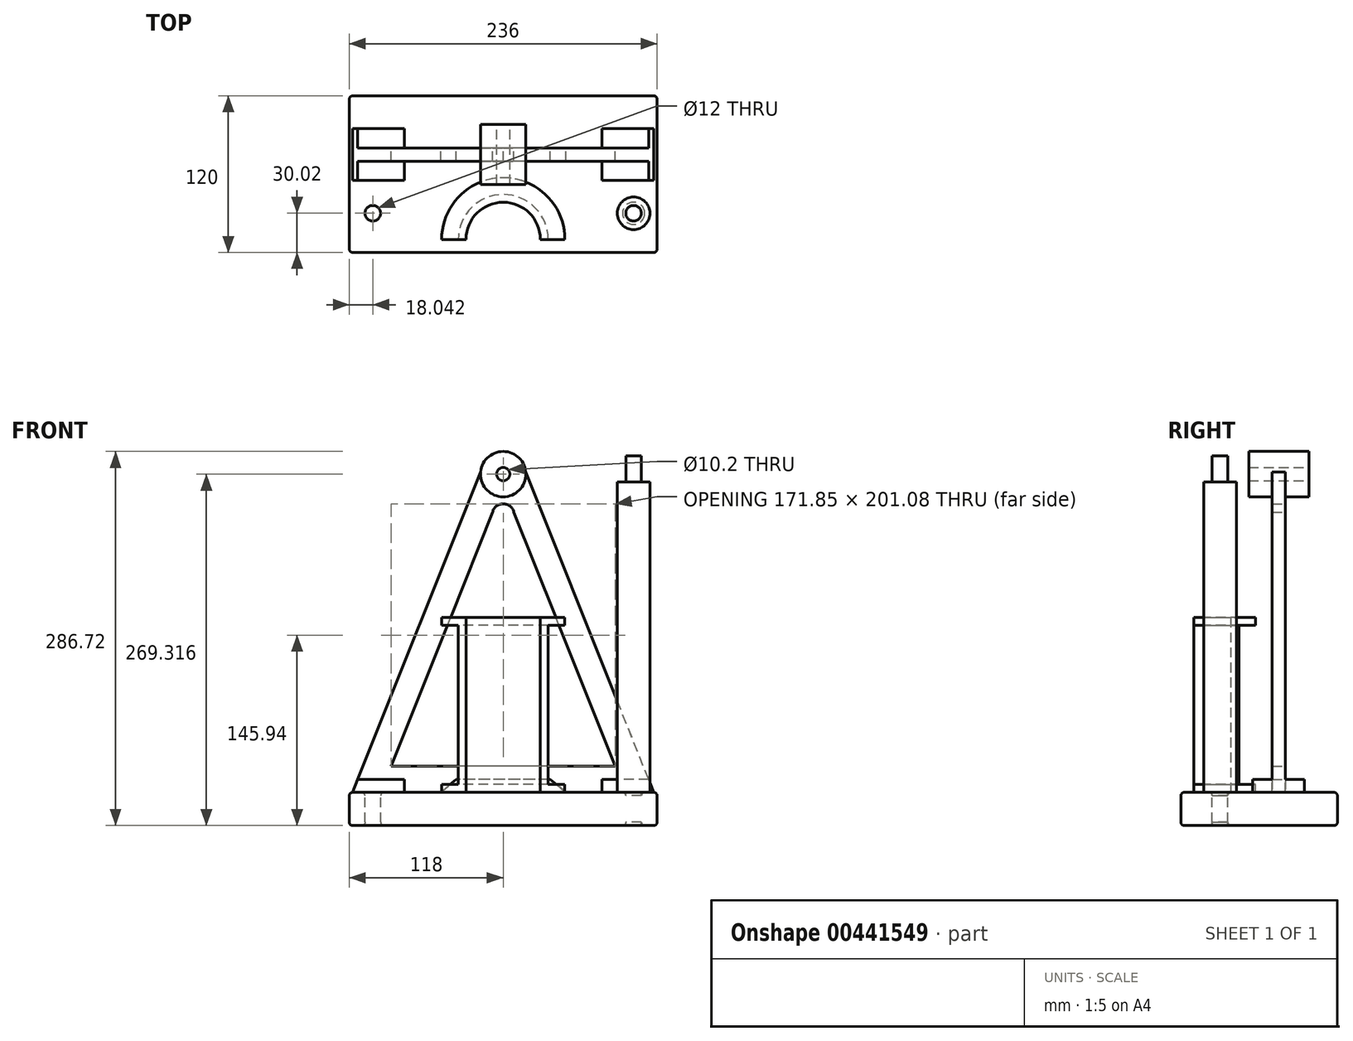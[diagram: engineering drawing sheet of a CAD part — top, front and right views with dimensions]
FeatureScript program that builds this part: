
annotation { "Feature Type Name" : "Feature", "Feature Type Description" : "" }
export const myFeature = defineFeature(function(context is Context, id is Id, definition is map)
    precondition{}
    {
        {
            var Q0;
            Q0=qCreatedBy(makeId("Top.planeOp"),FACE);
            var sketch = newSketch(context, id + "F0", { "sketchPlane" : qUnion([Q0])});
            skLineSegment(sketch, "E0.bottom", {"start": v(118, -60) * mm, "end": v(-118, -60) * mm});
            skLineSegment(sketch, "E0.top", {"start": v(118, 60) * mm, "end": v(-118, 60) * mm});
            skLineSegment(sketch, "E0.left", {"start": v(118, -60) * mm, "end": v(118, 60) * mm});
            skLineSegment(sketch, "E0.right", {"start": v(-118, -60) * mm, "end": v(-118, 60) * mm});
            skPoint(sketch, "E0.middle", {"position": v(0, 0) * mm});
            skSolve(sketch);
        }
        {
            var Q0;
            Q0 = qSketchRegion(id + "F0", true);
            extrude(context, id + "F1", {"entities" : qUnion([Q0]), "depth" : 25.4 * mm});
        }
        {
            var Q0;
            Q0=makeQuery(id+"F1.opExtrude","CAP_FACE",FACE,{"disambiguationData":[OSD([sQuery(id+"F0.wireOp",EDGE,"E0.bottom"),sQuery(id+"F0.wireOp",EDGE,"E0.top"),sQuery(id+"F0.wireOp",EDGE,"E0.left"),sQuery(id+"F0.wireOp",EDGE,"E0.right")])],"isStart":false});
            var sketch = newSketch(context, id + "F2", { "sketchPlane" : qUnion([Q0])});
            skCircle(sketch, "E1", {"center": v(-99.96, -29.98) * mm, "radius": 6 * mm});
            skCircle(sketch, "E2", {"center": v(99.96, -29.98) * mm, "radius": 6 * mm});
            skSolve(sketch);
        }
        {
            var Q0;
            Q0 = qSketchRegion(id + "F2", true);
            extrude(context, id + "F3", {"entities" : qUnion([Q0]), "operationType" : NewBodyOperationType.REMOVE, "oppositeDirection" : true, "depth" : 40.4 * mm});
        }
        {
            var Q0;
            Q0=makeQuery(id+"F1.opExtrude","CAP_EDGE",EDGE,{"disambiguationData":[OSD([sQuery(id+"F0.wireOp",EDGE,"E0.bottom")])],"isStart":false});
            var Q1;
            Q1=makeQuery(id+"F1.opExtrude","CAP_EDGE",EDGE,{"disambiguationData":[OSD([sQuery(id+"F0.wireOp",EDGE,"E0.left")])],"isStart":false});
            var Q2;
            Q2=makeQuery(id+"F1.opExtrude","CAP_EDGE",EDGE,{"disambiguationData":[OSD([sQuery(id+"F0.wireOp",EDGE,"E0.top")])],"isStart":false});
            var Q3;
            Q3=makeQuery(id+"F1.opExtrude","SWEPT_FACE",FACE,{"disambiguationData":[OSD([sQuery(id+"F0.wireOp",EDGE,"E0.bottom")])]});
            var Q4;
            Q4=makeQuery(id+"F1.opExtrude","CAP_FACE",FACE,{"disambiguationData":[OSD([sQuery(id+"F0.wireOp",EDGE,"E0.bottom"),sQuery(id+"F0.wireOp",EDGE,"E0.top"),sQuery(id+"F0.wireOp",EDGE,"E0.left"),sQuery(id+"F0.wireOp",EDGE,"E0.right")])],"isStart":true});
            var Q5;
            Q5=makeQuery(id+"F1.opExtrude","SWEPT_FACE",FACE,{"disambiguationData":[OSD([sQuery(id+"F0.wireOp",EDGE,"E0.right")])]});
            var Q6;
            Q6=makeQuery(id+"F1.opExtrude","SWEPT_FACE",FACE,{"disambiguationData":[OSD([sQuery(id+"F0.wireOp",EDGE,"E0.top")])]});
            var Q7;
            Q7=makeQuery(id+"F3.boolean.opBoolean","COPY",FACE,{"derivedFrom":makeQuery(id+"F3.opExtrude","SWEPT_FACE",FACE,{"disambiguationData":[OSD([sQuery(id+"F2.wireOp",EDGE,"E2")])]})});
            var Q8;
            Q8=makeQuery(id+"F3.boolean.opBoolean","COPY",FACE,{"derivedFrom":makeQuery(id+"F3.opExtrude","SWEPT_FACE",FACE,{"disambiguationData":[OSD([sQuery(id+"F2.wireOp",EDGE,"E1")])]})});
            fillet(context, id + "F4", {"entities" : qUnion([Q0, Q1, Q2, Q3, Q4, Q5, Q6, Q7, Q8]), "radius" : 2.54 * mm, "tangentPropagation" : true, "allowEdgeOverflow" : false});
        }
        {
            var Q0;
            Q0=makeQuery(id+"F1.opExtrude","SWEPT_FACE",FACE,{"disambiguationData":[OSD([sQuery(id+"F0.wireOp",EDGE,"E0.top")])]});
            cPlane(context, id + "F5", {"entities" : qUnion([Q0]), "cplaneType" : CPlaneType.OFFSET, "offset" : 40 * mm, "oppositeDirection" : true, "width" : 152.4 * mm, "height" : 152.4 * mm});
        }
        {
            var Q0;
            Q0=qCreatedBy(id+"F5.planeOp",FACE);
            var sketch = newSketch(context, id + "F6", { "sketchPlane" : qUnion([Q0])});
            skLineSegment(sketch, "E3.0", {"start": v(-115.46, 25.4) * mm, "end": v(115.46, 25.4) * mm});
            skArc(sketch, "E4.0", {"start": v(118, 22.86) * mm, "mid": v(117.26, 24.66) * mm, "end": v(115.46, 25.4) * mm});
            skLineSegment(sketch, "E5.0", {"start": v(118, 22.86) * mm, "end": v(118, 2.54) * mm});
            skLineSegment(sketch, "E6", {"start": v(-115.46, 25.4) * mm, "end": v(-17.33, 270.86) * mm});
            skLineSegment(sketch, "E7", {"start": v(-115.46, 25.4) * mm, "end": v(-47.96, 25.4) * mm});
            skLineSegment(sketch, "E8", {"start": v(-47.96, 25.4) * mm, "end": v(-36, 35.44) * mm});
            skLineSegment(sketch, "E9", {"start": v(-36, 35.44) * mm, "end": v(0, 35.44) * mm});
            skLineSegment(sketch, "E10", {"start": v(0, 330.43) * mm, "end": v(0, -58.87) * mm, "construction": true});
            skLineSegment(sketch, "E11", {"start": v(0, 35.44) * mm, "end": v(0, 25.4) * mm});
            skLineSegment(sketch, "E12", {"start": v(0, 25.4) * mm, "end": v(-47.96, 25.4) * mm});
            skPoint(sketch, "E13.orphan", {"position": v(0, 136.47) * mm});
            skLineSegment(sketch, "E14.MirrorCS", {"start": v(115.46, 25.4) * mm, "end": v(17.33, 270.86) * mm});
            skLineSegment(sketch, "E15.MirrorCS", {"start": v(115.46, 25.4) * mm, "end": v(47.96, 25.4) * mm});
            skLineSegment(sketch, "E16.MirrorCS", {"start": v(47.96, 25.4) * mm, "end": v(36, 35.44) * mm});
            skLineSegment(sketch, "E17.MirrorCS", {"start": v(36, 35.44) * mm, "end": v(0, 35.44) * mm});
            skLineSegment(sketch, "E18", {"start": v(0, 45.4) * mm, "end": v(-85.93, 45.4) * mm});
            skLineSegment(sketch, "E19", {"start": v(-85.93, 45.4) * mm, "end": v(-6.89, 243.1) * mm});
            skPoint(sketch, "E20", {"position": v(-8.05, 240.2) * mm});
            skArc(sketch, "E21", {"start": v(0, 246.48) * mm, "mid": v(-5.23, 244.89) * mm, "end": v(-8.05, 240.2) * mm});
            skLineSegment(sketch, "E22.MirrorCS", {"start": v(85.93, 45.4) * mm, "end": v(6.89, 243.1) * mm});
            skLineSegment(sketch, "E23.MirrorCS", {"start": v(0, 45.4) * mm, "end": v(85.93, 45.4) * mm});
            skArc(sketch, "E24.MirrorCS", {"start": v(0, 246.48) * mm, "mid": v(5.23, 244.89) * mm, "end": v(8.05, 240.2) * mm});
            skPoint(sketch, "E25", {"position": v(0, 269.32) * mm});
            skCircle(sketch, "E26", {"center": v(0, 269.32) * mm, "radius": 17.4 * mm});
            skCircle(sketch, "E27", {"center": v(0, 269.32) * mm, "radius": 5.1 * mm});
            skPoint(sketch, "E28.orphan", {"position": v(-13.62, 280.14) * mm});
            skPoint(sketch, "E29.orphan", {"position": v(13.62, 280.14) * mm});
            skLineSegment(sketch, "E30", {"start": v(-111.5, 35.3) * mm, "end": v(-75.6, 35.3) * mm});
            skLineSegment(sketch, "E31", {"start": v(-75.6, 35.3) * mm, "end": v(-75.6, 25.4) * mm});
            skLineSegment(sketch, "E32.MirrorCS", {"start": v(111.5, 35.3) * mm, "end": v(75.6, 35.3) * mm});
            skLineSegment(sketch, "E33.MirrorCS", {"start": v(75.6, 35.3) * mm, "end": v(75.6, 25.4) * mm});
            skSolve(sketch);
        }
        {
            var Q0;
            Q0=makeQuery(id+"F6.imprint","IMPRINT",FACE,{"disambiguationData":[TD([[makeQuery(id+"F6.imprint","IMPRINT",EDGE,{"derivedFrom":sQuery(id+"F6.wireOp",EDGE,"bef8d0ea-a7d9-4311-90df-f243bc0aed0c.0.0")}),1.0]])]});
            var Q1;
            Q1=makeQuery(id+"F6.imprint","IMPRINT",FACE,{"disambiguationData":[TD([[makeQuery(id+"F6.imprint","IMPRINT",EDGE,{"derivedFrom":sQuery(id+"F6.wireOp",EDGE,"E27")}),-1.0]])]});
            var Q2;
            {var subQ5=sQuery(id+"F6.wireOp",EDGE,"E6");Q2=makeQuery(id+"F6.imprint","IMPRINT",FACE,{"disambiguationData":[TD([[makeQuery(id+"F6.imprint","IMPRINT",EDGE,{"derivedFrom":subQ5}),-1.0]])]});}
            var Q3;
            {var subQ11=sQuery(id+"F6.wireOp",EDGE,"E8");Q3=makeQuery(id+"F6.imprint","IMPRINT",FACE,{"disambiguationData":[TD([[makeQuery(id+"F6.imprint","IMPRINT",EDGE,{"derivedFrom":subQ11}),1.0]])]});}
            var Q4;
            {var subQ3=sQuery(id+"F6.wireOp",EDGE,"E32.MirrorCS");Q4=makeQuery(id+"F6.imprint","IMPRINT",FACE,{"disambiguationData":[TD([[makeQuery(id+"F6.imprint","IMPRINT",EDGE,{"derivedFrom":subQ3}),1.0]])]});}
            extrude(context, id + "F7", {"entities" : qUnion([Q0, Q1, Q2, Q3, Q4]), "oppositeDirection" : true, "depth" : 10 * mm});
        }
        {
            var Q0;
            {var subQ3=sQuery(id+"F6.wireOp",EDGE,"E30");Q0=makeQuery(id+"F6.imprint","IMPRINT",FACE,{"disambiguationData":[TD([[makeQuery(id+"F6.imprint","IMPRINT",EDGE,{"derivedFrom":subQ3}),-1.0]])]});}
            var Q1;
            {var subQ3=sQuery(id+"F6.wireOp",EDGE,"E32.MirrorCS");Q1=makeQuery(id+"F6.imprint","IMPRINT",FACE,{"disambiguationData":[TD([[makeQuery(id+"F6.imprint","IMPRINT",EDGE,{"derivedFrom":subQ3}),1.0]])]});}
            extrude(context, id + "F8", {"entities" : qUnion([Q0, Q1]), "operationType" : NewBodyOperationType.ADD, "depth" : 14.8 * mm});
        }
        {
            var Q0;
            {var subQ3=sQuery(id+"F6.wireOp",EDGE,"E30");Q0=makeQuery(id+"F6.imprint","IMPRINT",FACE,{"disambiguationData":[TD([[makeQuery(id+"F6.imprint","IMPRINT",EDGE,{"derivedFrom":subQ3}),-1.0]])]});}
            var Q1;
            {var subQ3=sQuery(id+"F6.wireOp",EDGE,"E32.MirrorCS");Q1=makeQuery(id+"F6.imprint","IMPRINT",FACE,{"disambiguationData":[TD([[makeQuery(id+"F6.imprint","IMPRINT",EDGE,{"derivedFrom":subQ3}),1.0]])]});}
            extrude(context, id + "F9", {"entities" : qUnion([Q0, Q1]), "operationType" : NewBodyOperationType.ADD, "oppositeDirection" : true, "depth" : 24.9 * mm});
        }
        {
            var Q0;
            Q0=makeQuery(id+"F6.imprint","IMPRINT",FACE,{"disambiguationData":[TD([[makeQuery(id+"F6.imprint","IMPRINT",EDGE,{"derivedFrom":sQuery(id+"F6.wireOp",EDGE,"E27")}),-1.0]])]});
            extrude(context, id + "F10", {"entities" : qUnion([Q0]), "operationType" : NewBodyOperationType.ADD, "depth" : 18 * mm});
        }
        {
            var Q0;
            Q0=makeQuery(id+"F6.imprint","IMPRINT",FACE,{"disambiguationData":[TD([[makeQuery(id+"F6.imprint","IMPRINT",EDGE,{"derivedFrom":sQuery(id+"F6.wireOp",EDGE,"E27")}),-1.0]])]});
            extrude(context, id + "F11", {"entities" : qUnion([Q0]), "operationType" : NewBodyOperationType.ADD, "oppositeDirection" : true, "depth" : 27.94 * mm});
        }
        {
            var Q0;
            Q0=makeQuery(id+"F1.opExtrude","CAP_FACE",FACE,{"disambiguationData":[OSD([sQuery(id+"F0.wireOp",EDGE,"E0.bottom"),sQuery(id+"F0.wireOp",EDGE,"E0.top"),sQuery(id+"F0.wireOp",EDGE,"E0.left"),sQuery(id+"F0.wireOp",EDGE,"E0.right")])],"isStart":false});
            var sketch = newSketch(context, id + "F12", { "sketchPlane" : qUnion([Q0])});
            skCircle(sketch, "E34.0", {"center": v(99.96, -29.98) * mm, "radius": 6 * mm});
            skCircle(sketch, "E35", {"center": v(99.96, -29.98) * mm, "radius": 12.5 * mm});
            skSolve(sketch);
        }
        {
            var Q0;
            Q0 = qSketchRegion(id + "F12", true);
            var Q1;
            Q1=makeQuery(id+"F12.imprint","IMPRINT",FACE,{"disambiguationData":[TD([[makeQuery(id+"F12.imprint","IMPRINT",EDGE,{"derivedFrom":sQuery(id+"F12.wireOp",EDGE,"E34.0")}),1.0]])]});
            extrude(context, id + "F13", {"entities" : qUnion([Q0, Q1]), "depth" : 238 * mm});
        }
        {
            var Q0;
            Q0=makeQuery(id+"F12.imprint","IMPRINT",FACE,{"disambiguationData":[TD([[makeQuery(id+"F12.imprint","IMPRINT",EDGE,{"derivedFrom":sQuery(id+"F12.wireOp",EDGE,"E34.0")}),1.0]])]});
            var Q1;
            Q1=makeQuery(id+"F1.opExtrude","CAP_FACE",FACE,{"disambiguationData":[OSD([sQuery(id+"F0.wireOp",EDGE,"E0.bottom"),sQuery(id+"F0.wireOp",EDGE,"E0.top"),sQuery(id+"F0.wireOp",EDGE,"E0.left"),sQuery(id+"F0.wireOp",EDGE,"E0.right")])],"isStart":true});
            extrude(context, id + "F14", {"entities" : qUnion([Q0]), "operationType" : NewBodyOperationType.ADD, "endBound" : BoundingType.UP_TO_SURFACE, "oppositeDirection" : true, "endBoundEntityFace" : qUnion([Q1]), "depth" : 25.4 * mm});
        }
        {
            var Q0;
            Q0=makeQuery(id+"F13.opExtrude","CAP_FACE",FACE,{"disambiguationData":[OSD([sQuery(id+"F12.wireOp",EDGE,"E35")])],"isStart":false});
            var sketch = newSketch(context, id + "F15", { "sketchPlane" : qUnion([Q0])});
            skCircle(sketch, "E36.0", {"center": v(99.96, -29.98) * mm, "radius": 6 * mm});
            skSolve(sketch);
        }
        {
            var Q0;
            Q0 = qSketchRegion(id + "F15", true);
            extrude(context, id + "F16", {"entities" : qUnion([Q0]), "operationType" : NewBodyOperationType.ADD, "depth" : 20 * mm});
        }
        {
            var Q0;
            Q0=makeQuery(id+"F1.opExtrude","SWEPT_FACE",FACE,{"disambiguationData":[OSD([sQuery(id+"F0.wireOp",EDGE,"E0.bottom")])]});
            cPlane(context, id + "F17", {"entities" : qUnion([Q0]), "cplaneType" : CPlaneType.OFFSET, "offset" : 10 * mm, "oppositeDirection" : true, "width" : 152.4 * mm, "height" : 152.4 * mm});
        }
        {
            var Q0;
            Q0=qCreatedBy(id+"F17.planeOp",FACE);
            var sketch = newSketch(context, id + "F18", { "sketchPlane" : qUnion([Q0])});
            skLineSegment(sketch, "E37", {"start": v(0, 80.14) * mm, "end": v(0, -97.52) * mm, "construction": true});
            skLineSegment(sketch, "E38.0", {"start": v(-115.46, 25.4) * mm, "end": v(115.46, 25.4) * mm});
            skPoint(sketch, "E39.0.end.orphan", {"position": v(-118, 22.86) * mm});
            skPoint(sketch, "E39.0.start.orphan", {"position": v(-118, 2.54) * mm});
            skPoint(sketch, "E40.0.end.orphan", {"position": v(118, 2.54) * mm});
            skPoint(sketch, "E40.0.start.orphan", {"position": v(118, 22.86) * mm});
            skLineSegment(sketch, "E41", {"start": v(-47.25, 25.4) * mm, "end": v(-47.25, 31.4) * mm});
            skLineSegment(sketch, "E42", {"start": v(-47.25, 31.4) * mm, "end": v(-34.45, 31.4) * mm});
            skLineSegment(sketch, "E43", {"start": v(-34.45, 31.4) * mm, "end": v(-34.45, 153.4) * mm});
            skLineSegment(sketch, "E44", {"start": v(-34.45, 153.4) * mm, "end": v(-47.25, 153.4) * mm});
            skLineSegment(sketch, "E45", {"start": v(-47.25, 153.4) * mm, "end": v(-47.25, 159.4) * mm});
            skLineSegment(sketch, "E46", {"start": v(-47.25, 159.4) * mm, "end": v(-28.45, 159.4) * mm});
            skLineSegment(sketch, "E47", {"start": v(-28.45, 159.4) * mm, "end": v(-28.45, 25.4) * mm});
            skLineSegment(sketch, "E48", {"start": v(-28.45, 25.4) * mm, "end": v(-47.25, 25.4) * mm});
            skSolve(sketch);
        }
        {
            var Q0;
            Q0 = qSketchRegion(id + "F18", true);
            var Q1;
            Q1=sQuery(id+"F18.wireOp",EDGE,"E37");
            revolve(context, id + "F19", {"entities" : qUnion([Q0]), "axis" : qUnion([Q1]), "revolveType" : RevolveType.ONE_DIRECTION, "angle" : 180 * degree});
        }
    });
